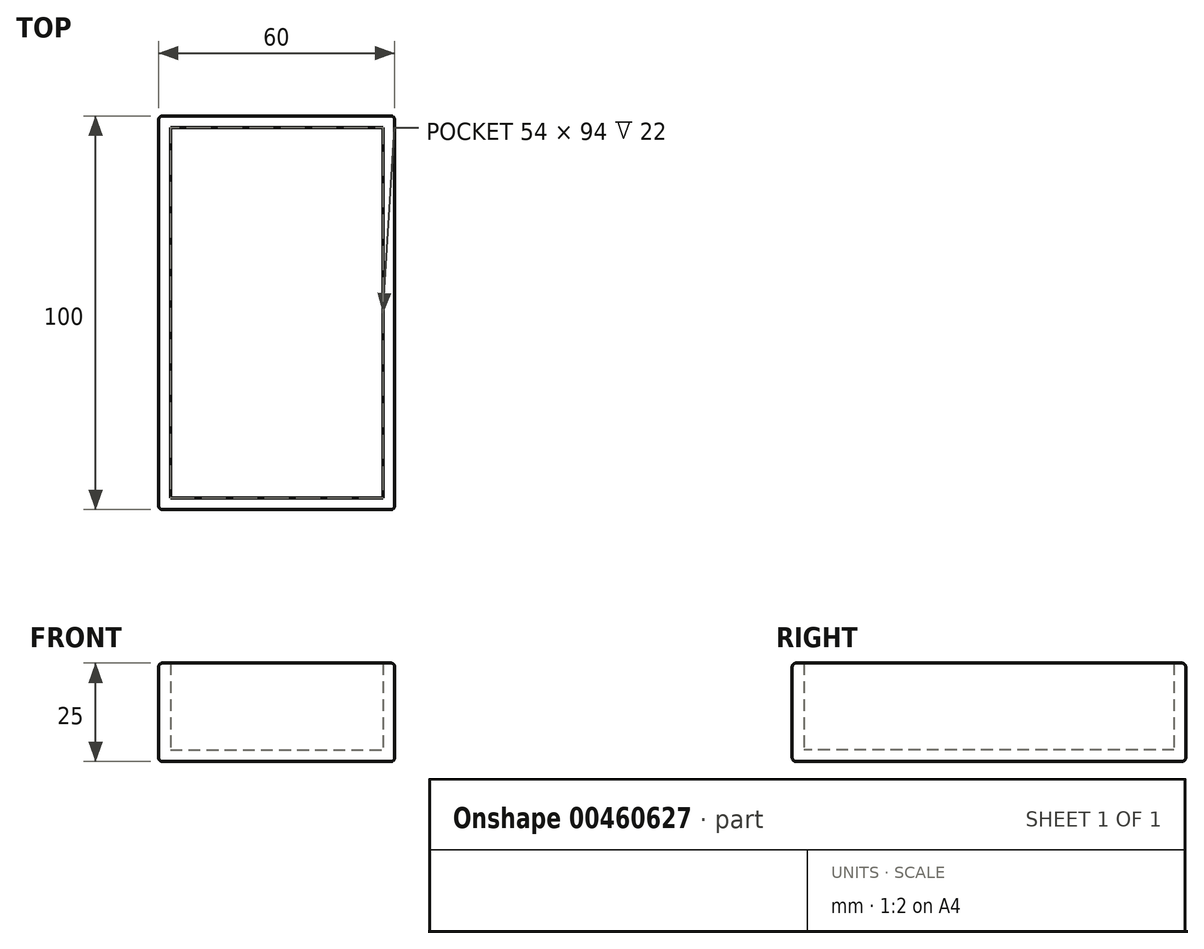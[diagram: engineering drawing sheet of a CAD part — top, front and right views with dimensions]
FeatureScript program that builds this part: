
annotation { "Feature Type Name" : "Feature", "Feature Type Description" : "" }
export const myFeature = defineFeature(function(context is Context, id is Id, definition is map)
    precondition{}
    {
        {
            var Q0;
            Q0=qCreatedBy(makeId("Top.planeOp"),FACE);
            var sketch = newSketch(context, id + "F0", { "sketchPlane" : qUnion([Q0])});
            skLineSegment(sketch, "E0.bottom", {"start": v(-46.97, 50.55) * mm, "end": v(13.03, 50.55) * mm});
            skLineSegment(sketch, "E0.top", {"start": v(-46.97, -49.45) * mm, "end": v(13.03, -49.45) * mm});
            skLineSegment(sketch, "E0.left", {"start": v(-46.97, 50.55) * mm, "end": v(-46.97, -49.45) * mm});
            skLineSegment(sketch, "E0.right", {"start": v(13.03, 50.55) * mm, "end": v(13.03, -49.45) * mm});
            skSolve(sketch);
        }
        {
            var Q0;
            Q0=makeQuery(id+"F0.imprint","IMPRINT",FACE,{"disambiguationData":[TD([[makeQuery(id+"F0.imprint","IMPRINT",EDGE,{"derivedFrom":sQuery(id+"F0.wireOp",EDGE,"E0.bottom")}),-1.0]])]});
            extrude(context, id + "F1", {"entities" : qUnion([Q0]), "depth" : 25 * mm});
        }
        {
            var Q0;
            Q0=makeQuery(id+"F1.opExtrude","CAP_FACE",FACE,{"disambiguationData":[OSD([sQuery(id+"F0.wireOp",EDGE,"E0.bottom"),sQuery(id+"F0.wireOp",EDGE,"E0.top"),sQuery(id+"F0.wireOp",EDGE,"E0.left"),sQuery(id+"F0.wireOp",EDGE,"E0.right")])],"isStart":false});
            shell(context, id + "F2", {"entities" : qUnion([Q0]), "thickness" : 3 * mm});
        }
        {
            var Q0;
            Q0=makeQuery(id+"F1.opExtrude","CAP_EDGE",EDGE,{"disambiguationData":[OSD([sQuery(id+"F0.wireOp",EDGE,"E0.right")])],"isStart":false});
            var Q1;
            Q1=makeQuery(id+"F1.opExtrude","CAP_EDGE",EDGE,{"disambiguationData":[OSD([sQuery(id+"F0.wireOp",EDGE,"E0.top")])],"isStart":false});
            var Q2;
            Q2=makeQuery(id+"F1.opExtrude","CAP_EDGE",EDGE,{"disambiguationData":[OSD([sQuery(id+"F0.wireOp",EDGE,"E0.left")])],"isStart":false});
            var Q3;
            Q3=makeQuery(id+"F1.opExtrude","CAP_EDGE",EDGE,{"disambiguationData":[OSD([sQuery(id+"F0.wireOp",EDGE,"E0.bottom")])],"isStart":false});
            var Q4;
            Q4=makeQuery(id+"F1.opExtrude","SWEPT_EDGE",EDGE,{"disambiguationData":[OSD([sQuery(id+"F0.wireOp",EDGE,"E0.bottom"),sQuery(id+"F0.wireOp",EDGE,"E0.right")])]});
            var Q5;
            Q5=makeQuery(id+"F1.opExtrude","SWEPT_EDGE",EDGE,{"disambiguationData":[OSD([sQuery(id+"F0.wireOp",EDGE,"E0.top"),sQuery(id+"F0.wireOp",EDGE,"E0.right")])]});
            var Q6;
            Q6=makeQuery(id+"F1.opExtrude","SWEPT_FACE",FACE,{"disambiguationData":[OSD([sQuery(id+"F0.wireOp",EDGE,"E0.top")])]});
            var Q7;
            Q7=makeQuery(id+"F1.opExtrude","CAP_FACE",FACE,{"disambiguationData":[OSD([sQuery(id+"F0.wireOp",EDGE,"E0.bottom"),sQuery(id+"F0.wireOp",EDGE,"E0.top"),sQuery(id+"F0.wireOp",EDGE,"E0.left"),sQuery(id+"F0.wireOp",EDGE,"E0.right")])],"isStart":true});
            var Q8;
            Q8=makeQuery(id+"F1.opExtrude","SWEPT_FACE",FACE,{"disambiguationData":[OSD([sQuery(id+"F0.wireOp",EDGE,"E0.left")])]});
            fillet(context, id + "F3", {"entities" : qUnion([Q0, Q1, Q2, Q3, Q4, Q5, Q6, Q7, Q8]), "radius" : 1 * mm, "tangentPropagation" : true, "allowEdgeOverflow" : false});
        }
    });
